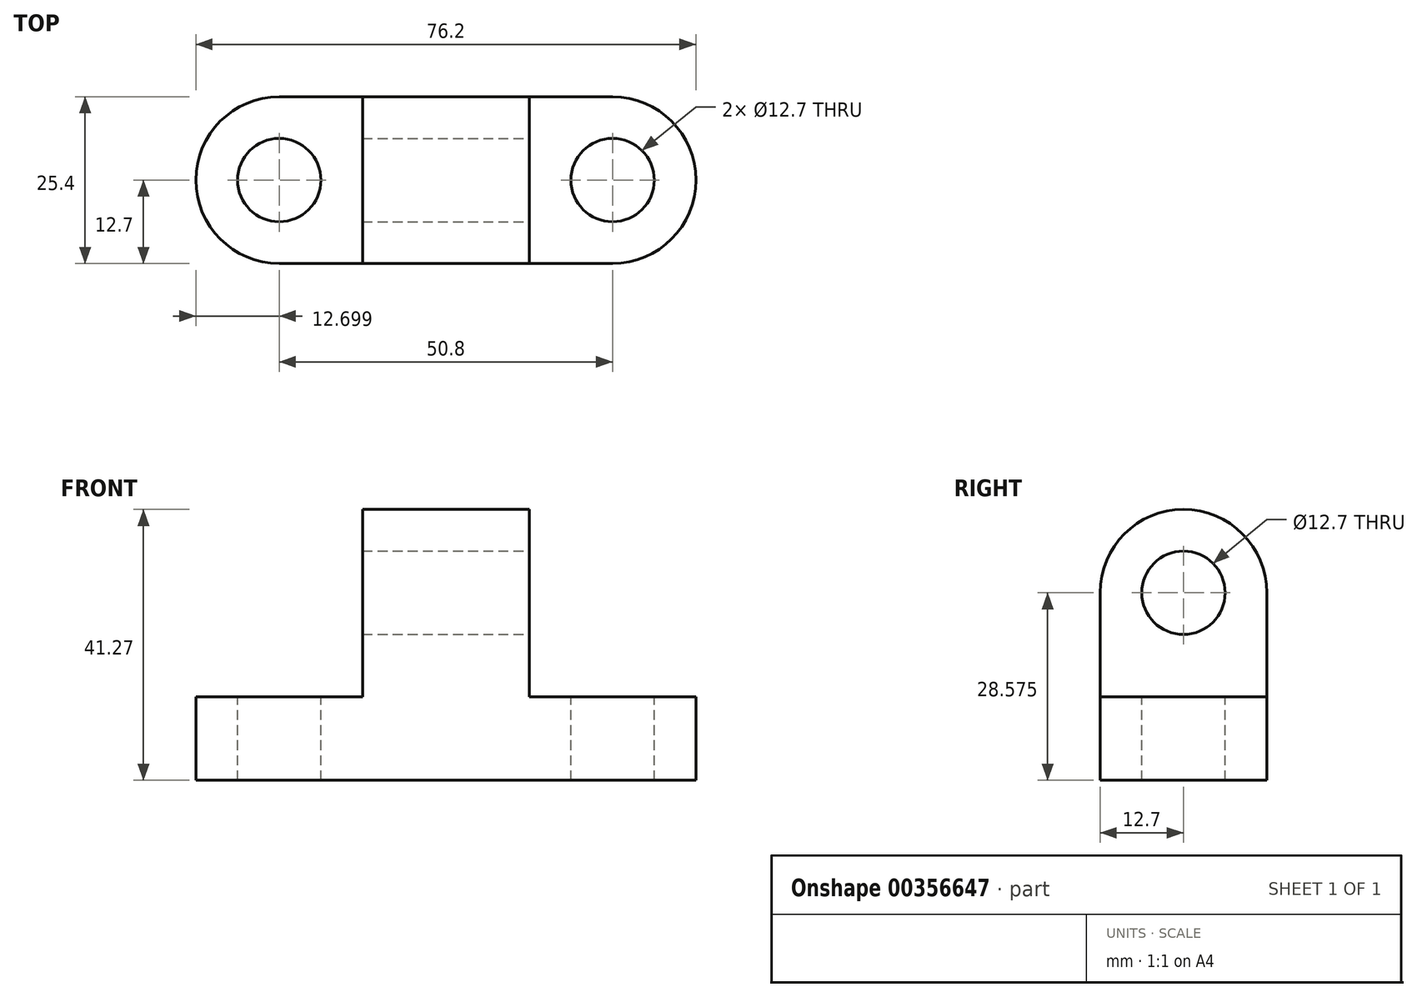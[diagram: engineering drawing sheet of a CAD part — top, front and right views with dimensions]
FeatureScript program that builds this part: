
annotation { "Feature Type Name" : "Feature", "Feature Type Description" : "" }
export const myFeature = defineFeature(function(context is Context, id is Id, definition is map)
    precondition{}
    {
        {
            var Q0;
            Q0=qCreatedBy(makeId("Front.planeOp"),FACE);
            var sketch = newSketch(context, id + "F0", { "sketchPlane" : qUnion([Q0])});
            skLineSegment(sketch, "E0", {"start": v(-33.77, 0) * mm, "end": v(42.43, 0) * mm});
            skLineSegment(sketch, "E1", {"start": v(42.43, 0) * mm, "end": v(42.43, 12.7) * mm});
            skLineSegment(sketch, "E2", {"start": v(42.43, 12.7) * mm, "end": v(17.03, 12.7) * mm});
            skLineSegment(sketch, "E3", {"start": v(17.03, 12.7) * mm, "end": v(17.03, 44.45) * mm});
            skLineSegment(sketch, "E4", {"start": v(17.03, 44.45) * mm, "end": v(-8.37, 44.45) * mm});
            skLineSegment(sketch, "E5", {"start": v(-8.37, 44.45) * mm, "end": v(-8.37, 12.7) * mm});
            skLineSegment(sketch, "E6", {"start": v(-8.37, 12.7) * mm, "end": v(-33.77, 12.7) * mm});
            skLineSegment(sketch, "E7", {"start": v(-33.77, 12.7) * mm, "end": v(-33.77, 0) * mm});
            skSolve(sketch);
        }
        {
            var Q0;
            Q0 = qSketchRegion(id + "F0", true);
            extrude(context, id + "F1", {"entities" : qUnion([Q0]), "depth" : 25.4 * mm});
        }
        {
            var Q0;
            Q0=makeQuery(id+"F1.opExtrude","SWEPT_FACE",FACE,{"disambiguationData":[OSD([sQuery(id+"F0.wireOp",EDGE,"E3")])]});
            var sketch = newSketch(context, id + "F2", { "sketchPlane" : qUnion([Q0])});
            skPoint(sketch, "E8.centerSnap0", {"position": v(-12.7, 12.7) * mm});
            skPoint(sketch, "E8.centerSnap1", {"position": v(-25.4, 28.58) * mm});
            skCircle(sketch, "E9", {"center": v(-12.7, 28.58) * mm, "radius": 12.7 * mm});
            skPoint(sketch, "E9.centerSnap0", {"position": v(0, 28.58) * mm});
            skSolve(sketch);
        }
        {
            var Q0;
            {var subQ1=sQuery(id+"F0.wireOp",EDGE,"E3");var subQ6=makeQuery(id+"F1.opExtrude","SWEPT_EDGE",EDGE,{"disambiguationData":[OSD([subQ1,sQuery(id+"F0.wireOp",EDGE,"E4")])]});Q0=makeQuery(id+"F2.imprint","IMPRINT",FACE,{"disambiguationData":[TD([[makeQuery(id+"F2.imprint","IMPRINT",EDGE,{"derivedFrom":subQ6}),-1.0]])]});}
            extrude(context, id + "F3", {"entities" : qUnion([Q0]), "operationType" : NewBodyOperationType.REMOVE, "oppositeDirection" : true, "depth" : 25.4 * mm});
        }
        {
            var Q0;
            Q0=makeQuery(id+"F1.opExtrude","SWEPT_FACE",FACE,{"disambiguationData":[OSD([sQuery(id+"F0.wireOp",EDGE,"E3")])]});
            var sketch = newSketch(context, id + "F4", { "sketchPlane" : qUnion([Q0])});
            skCircle(sketch, "E10", {"center": v(-12.7, 28.58) * mm, "radius": 6.35 * mm});
            skSolve(sketch);
        }
        {
            var Q0;
            Q0 = qSketchRegion(id + "F4", true);
            extrude(context, id + "F5", {"entities" : qUnion([Q0]), "operationType" : NewBodyOperationType.REMOVE, "oppositeDirection" : true, "depth" : 25.4 * mm});
        }
        {
            var Q0;
            Q0=makeQuery(id+"F1.opExtrude","SWEPT_FACE",FACE,{"disambiguationData":[OSD([sQuery(id+"F0.wireOp",EDGE,"E2")])]});
            var sketch = newSketch(context, id + "F6", { "sketchPlane" : qUnion([Q0])});
            skCircle(sketch, "E11", {"center": v(29.73, -12.7) * mm, "radius": 12.7 * mm});
            skPoint(sketch, "E11.centerSnap0", {"position": v(42.43, -12.7) * mm});
            skPoint(sketch, "E11.centerSnap1", {"position": v(29.73, 0) * mm});
            skSolve(sketch);
        }
        {
            var Q0;
            {var subQ0=sQuery(id+"F6.wireOp",EDGE,"E11");var subQ1=sQuery(id+"F0.wireOp",EDGE,"E2");var subQ2=makeQuery(id+"F1.opExtrude","CAP_EDGE",EDGE,{"disambiguationData":[OSD([subQ1])],"isStart":true});var subQ3=makeQuery(id+"F6.imprint","INTERSECT",VERTEX,{"derivedFrom":[subQ2,subQ0]});Q0=makeQuery(id+"F6.imprint","IMPRINT",FACE,{"disambiguationData":[TD([[makeQuery(id+"F6.imprint","IMPRINT",EDGE,{"disambiguationData":[TD([[subQ3,1.0]])],"derivedFrom":subQ0}),-1.0]])]});}
            var Q1;
            {var subQ0=sQuery(id+"F6.wireOp",EDGE,"E11");var subQ1=sQuery(id+"F0.wireOp",EDGE,"E2");var subQ4=makeQuery(id+"F1.opExtrude","CAP_EDGE",EDGE,{"disambiguationData":[OSD([subQ1])],"isStart":false});var subQ5=makeQuery(id+"F6.imprint","INTERSECT",VERTEX,{"derivedFrom":[subQ4,subQ0]});Q1=makeQuery(id+"F6.imprint","IMPRINT",FACE,{"disambiguationData":[TD([[makeQuery(id+"F6.imprint","IMPRINT",EDGE,{"disambiguationData":[TD([[subQ5,-1.0]])],"derivedFrom":subQ0}),-1.0]])]});}
            extrude(context, id + "F7", {"entities" : qUnion([Q0, Q1]), "operationType" : NewBodyOperationType.REMOVE, "oppositeDirection" : true, "depth" : 25.4 * mm});
        }
        {
            var Q0;
            Q0=makeQuery(id+"F1.opExtrude","SWEPT_FACE",FACE,{"disambiguationData":[OSD([sQuery(id+"F0.wireOp",EDGE,"E6")])]});
            var sketch = newSketch(context, id + "F8", { "sketchPlane" : qUnion([Q0])});
            skCircle(sketch, "E12", {"center": v(-21.07, -12.7) * mm, "radius": 12.7 * mm});
            skPoint(sketch, "E12.centerSnap0", {"position": v(-21.07, 0) * mm});
            skPoint(sketch, "E12.centerSnap1", {"position": v(-33.77, -12.7) * mm});
            skSolve(sketch);
        }
        {
            var Q0;
            {var subQ0=sQuery(id+"F8.wireOp",EDGE,"E12");var subQ1=sQuery(id+"F0.wireOp",EDGE,"E6");var subQ2=makeQuery(id+"F1.opExtrude","CAP_EDGE",EDGE,{"disambiguationData":[OSD([subQ1])],"isStart":true});var subQ3=makeQuery(id+"F8.imprint","INTERSECT",VERTEX,{"derivedFrom":[subQ2,subQ0]});Q0=makeQuery(id+"F8.imprint","IMPRINT",FACE,{"disambiguationData":[TD([[makeQuery(id+"F8.imprint","IMPRINT",EDGE,{"disambiguationData":[TD([[subQ3,-1.0]])],"derivedFrom":subQ0}),-1.0]])]});}
            var Q1;
            {var subQ0=sQuery(id+"F8.wireOp",EDGE,"E12");var subQ1=sQuery(id+"F0.wireOp",EDGE,"E6");var subQ4=makeQuery(id+"F1.opExtrude","CAP_EDGE",EDGE,{"disambiguationData":[OSD([subQ1])],"isStart":false});var subQ5=makeQuery(id+"F8.imprint","INTERSECT",VERTEX,{"derivedFrom":[subQ4,subQ0]});Q1=makeQuery(id+"F8.imprint","IMPRINT",FACE,{"disambiguationData":[TD([[makeQuery(id+"F8.imprint","IMPRINT",EDGE,{"disambiguationData":[TD([[subQ5,1.0]])],"derivedFrom":subQ0}),-1.0]])]});}
            extrude(context, id + "F9", {"entities" : qUnion([Q0, Q1]), "operationType" : NewBodyOperationType.REMOVE, "oppositeDirection" : true, "depth" : 25.4 * mm});
        }
        {
            var Q0;
            Q0=makeQuery(id+"F1.opExtrude","SWEPT_FACE",FACE,{"disambiguationData":[OSD([sQuery(id+"F0.wireOp",EDGE,"E6")])]});
            var sketch = newSketch(context, id + "F10", { "sketchPlane" : qUnion([Q0])});
            skCircle(sketch, "E13", {"center": v(-21.07, -12.7) * mm, "radius": 6.35 * mm});
            skSolve(sketch);
        }
        {
            var Q0;
            Q0 = qSketchRegion(id + "F10", true);
            extrude(context, id + "F11", {"entities" : qUnion([Q0]), "operationType" : NewBodyOperationType.REMOVE, "oppositeDirection" : true, "depth" : 25.4 * mm});
        }
        {
            var Q0;
            Q0=makeQuery(id+"F1.opExtrude","SWEPT_FACE",FACE,{"disambiguationData":[OSD([sQuery(id+"F0.wireOp",EDGE,"E2")])]});
            var sketch = newSketch(context, id + "F12", { "sketchPlane" : qUnion([Q0])});
            skCircle(sketch, "E14", {"center": v(29.73, -12.7) * mm, "radius": 6.35 * mm});
            skSolve(sketch);
        }
        {
            var Q0;
            Q0 = qSketchRegion(id + "F12", true);
            extrude(context, id + "F13", {"entities" : qUnion([Q0]), "operationType" : NewBodyOperationType.REMOVE, "oppositeDirection" : true, "depth" : 25.4 * mm});
        }
    });
